FCSTD DOCUMENT  (FreeCAD 0.14R3702 (Git))
Label: wheel
License: CC-BY 3.0
LicenseURL: http://creativecommons.org/licenses/by/3.0/
objects: Sketcher::SketchObject×3, Part::FeaturePython×2
note: 5 computed .brp shape members not serialized (recipe doc carries the construction recipe); baked Part::Feature solids carry a one-line shape summary decoded from their .brp

FEATURE [Sketcher::SketchObject] Sketch
  sketch-geometry (5):
    g0: Circle CenterX=0 CenterY=0 CenterZ=0 NormalX=0 NormalY=0 NormalZ=1 Radius=20
    g1: LineSegment StartX=-14.1421 StartY=-14.1421 StartZ=0 EndX=14.1421 EndY=14.1421 EndZ=0
    g2: LineSegment StartX=-14.1421 StartY=14.1421 StartZ=0 EndX=14.1421 EndY=-14.1421 EndZ=0
    g3: LineSegment StartX=0 StartY=20 StartZ=0 EndX=0 EndY=-20 EndZ=0
    g4: LineSegment StartX=-20 StartY=0 StartZ=0 EndX=20 EndY=0 EndZ=0
  constraints (18):
    c: Radius(g0) = 20
    c: PointOnObject(g1,g0)
    c: Coincident(g0,g-1)
    c: PointOnObject(g1,g0)
    c: Angle(g1) = 0.785398
    c: PointOnObject(g-1,g1)
    c: PointOnObject(g2,g0)
    c: PointOnObject(g3,g0)
    c: Vertical(g3)
    c: Horizontal(g4)
    c: PointOnObject(g-1,g2)
    c: Angle(g2) = -0.785398
    c: PointOnObject(g3,g0)
    c: PointOnObject(g-1,g3)
    c: PointOnObject(g4,g0)
    c: PointOnObject(g4,g0)
    c: PointOnObject(g-1,g4)
    c: PointOnObject(g2,g0)
FEATURE [Sketcher::SketchObject] Sketch001
  Placement = pos=(-2,0,0) rot=(0,0,1;0.392699rad)
  sketch-geometry (6):
    g0: ArcOfCircle CenterX=0 CenterY=0 CenterZ=0 NormalX=0 NormalY=0 NormalZ=1 Radius=20 StartAngle=2.35619 EndAngle=3.14159
    g1: LineSegment StartX=-14.1421 StartY=14.1421 StartZ=0 EndX=0 EndY=0 EndZ=0
    g2: LineSegment StartX=-20 StartY=0 StartZ=0 EndX=0 EndY=0 EndZ=0
    g3: Circle CenterX=-15.296 CenterY=6.33582 CenterZ=0 NormalX=0 NormalY=0 NormalZ=1 Radius=0
    g4: LineSegment [constr] StartX=-15.296 StartY=6.33582 StartZ=0 EndX=0 EndY=0 EndZ=0
    g5: Circle CenterX=-15.296 CenterY=6.33582 CenterZ=0 NormalX=0 NormalY=0 NormalZ=1 Radius=0.05
  constraints (15):
    c: Coincident(g0,g-1)
    c: Distance(g-1,g0) = 20
    c: Coincident(g1,g0)
    c: Coincident(g2,g0)
    c: Coincident(g0,g1)
    c: Coincident(g0,g2)
    c: Horizontal(g2)
    c: Angle(g1,g2) = 0.785398
    c: DistanceY(g-1,g3) = 6.33582
    c: Coincident(g4,g3)
    c: Coincident(g4,g-1)
    c: Tangent(g4,g3)
    c: Angle(g4) = -0.392699
    c: Coincident(g5,g3)
    c: Radius(g5) = 0.05
FEATURE [Part::FeaturePython] Array  # Draft array (typed FeaturePython)
  Angle = 360
  ArrayType = 1
  Axis = (0,0,1)
  Base = -> Sketch001
  Center = (0,0,0)
  IntervalX = (1,0,0)
  IntervalY = (0,1,0)
  IntervalZ = (0,0,1)
  NumberPolar = 8
  NumberX = 2
  NumberY = 2
  NumberZ = 1
FEATURE [Sketcher::SketchObject] Sketch002
  Placement = pos=(-1,0,0) rot=(0,0,1;0.392699rad)
  sketch-geometry (6):
    g0: ArcOfCircle CenterX=0 CenterY=0 CenterZ=0 NormalX=0 NormalY=0 NormalZ=1 Radius=9 StartAngle=2.35619 EndAngle=3.14159
    g1: LineSegment StartX=-6.36396 StartY=6.36396 StartZ=0 EndX=0 EndY=0 EndZ=0
    g2: LineSegment StartX=-9 StartY=0 StartZ=0 EndX=0 EndY=0 EndZ=0
    g3: Circle CenterX=-6.46716 CenterY=2.67878 CenterZ=0 NormalX=0 NormalY=0 NormalZ=1 Radius=0
    g4: LineSegment [constr] StartX=-6.46716 StartY=2.67878 StartZ=0 EndX=0 EndY=0 EndZ=0
    g5: Circle CenterX=-6.46716 CenterY=2.67878 CenterZ=0 NormalX=0 NormalY=0 NormalZ=1 Radius=0.05
  constraints (15):
    c: Coincident(g0,g-1)
    c: Distance(g-1,g0) = 9
    c: Coincident(g1,g0)
    c: Coincident(g2,g0)
    c: Coincident(g0,g1)
    c: Coincident(g0,g2)
    c: Horizontal(g2)
    c: Angle(g1,g2) = 0.785398
    c: Coincident(g4,g3)
    c: Coincident(g4,g-1)
    c: Tangent(g4,g3)
    c: Angle(g4) = -0.392699
    c: Coincident(g5,g3)
    c: Radius(g5) = 0.05
    c: Distance(g4) = 7
FEATURE [Part::FeaturePython] Array001  # Draft array (typed FeaturePython)
  Angle = 360
  ArrayType = 1
  Axis = (0,0,1)
  Base = -> Sketch002
  Center = (0,0,0)
  IntervalX = (1,0,0)
  IntervalY = (0,1,0)
  IntervalZ = (0,0,1)
  NumberPolar = 8
  NumberX = 2
  NumberY = 2
  NumberZ = 1
